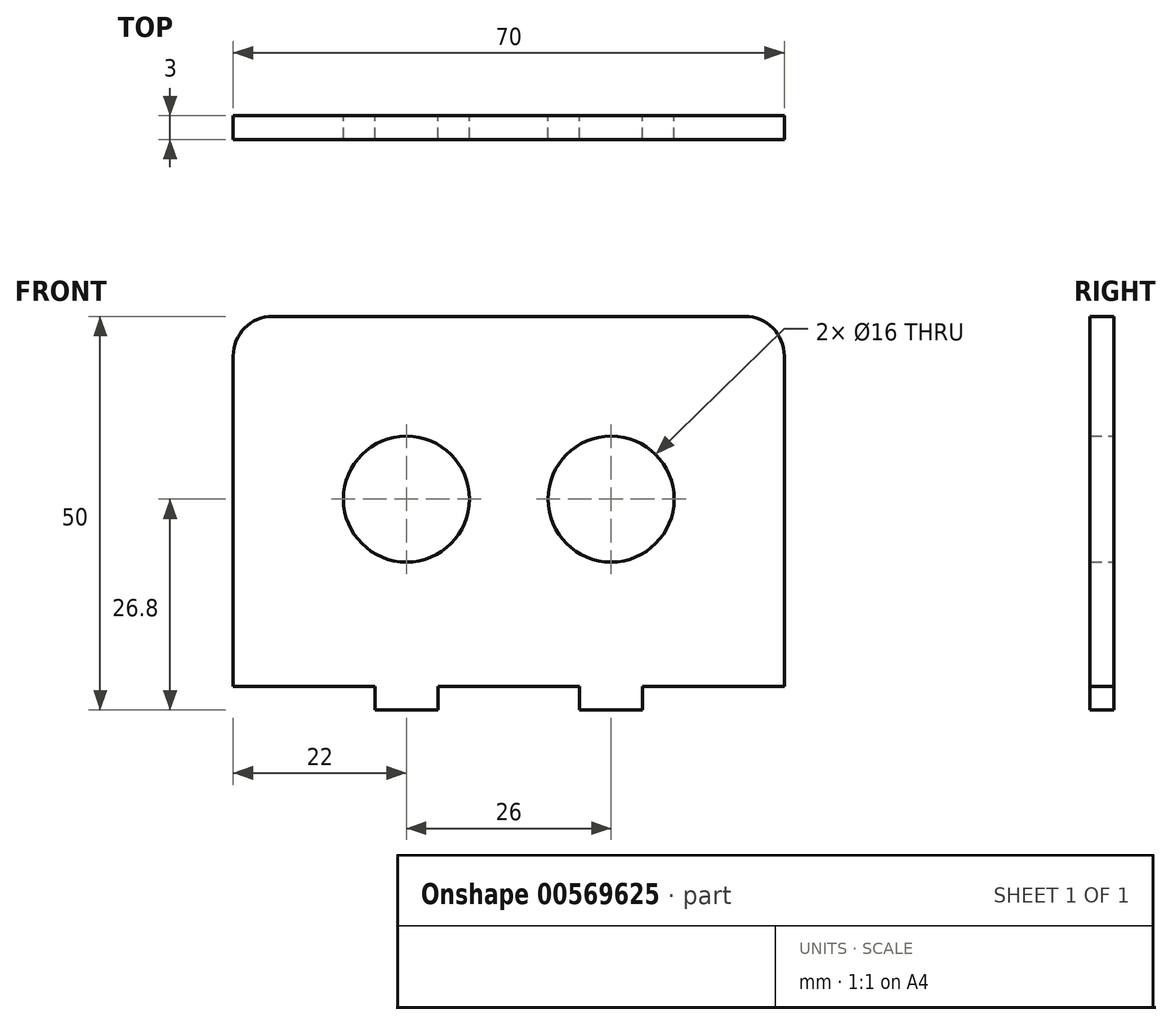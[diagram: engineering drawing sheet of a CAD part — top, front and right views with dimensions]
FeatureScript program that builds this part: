
annotation { "Feature Type Name" : "Feature", "Feature Type Description" : "" }
export const myFeature = defineFeature(function(context is Context, id is Id, definition is map)
    precondition{}
    {
        {
            var Q0;
            Q0=qCreatedBy(makeId("Front.planeOp"),FACE);
            var sketch = newSketch(context, id + "F0", { "sketchPlane" : qUnion([Q0])});
            skLineSegment(sketch, "E0.bottom", {"start": v(-34, 23.2) * mm, "end": v(26, 23.2) * mm});
            skLineSegment(sketch, "E0.top", {"start": v(-21, -26.8) * mm, "end": v(-13, -26.8) * mm});
            skLineSegment(sketch, "E0.left", {"start": v(-39, 18.2) * mm, "end": v(-39, -23.8) * mm});
            skLineSegment(sketch, "E0.right", {"start": v(31, 18.2) * mm, "end": v(31, -26.8) * mm});
            skCircle(sketch, "E1", {"center": v(-17, 0) * mm, "radius": 8 * mm});
            skCircle(sketch, "E2", {"center": v(9, 0) * mm, "radius": 8 * mm});
            skPoint(sketch, "E3.visualSharp", {"position": v(-39, 23.2) * mm});
            skArc(sketch, "E3.filletArc", {"start": v(-34, 23.2) * mm, "mid": v(-37.54, 21.74) * mm, "end": v(-39, 18.2) * mm});
            skPoint(sketch, "E4.visualSharp", {"position": v(31, 23.2) * mm});
            skArc(sketch, "E4.filletArc", {"start": v(31, 18.2) * mm, "mid": v(29.54, 21.74) * mm, "end": v(26, 23.2) * mm});
            skLineSegment(sketch, "E5", {"start": v(45.92, -19.01) * mm, "end": v(45.92, -19.01) * mm});
            skLineSegment(sketch, "E6", {"start": v(-44.57, -23.8) * mm, "end": v(-21, -23.8) * mm, "construction": true});
            skLineSegment(sketch, "E7", {"start": v(-21, -23.8) * mm, "end": v(-21, -26.8) * mm});
            skLineSegment(sketch, "E8", {"start": v(-13, -23.8) * mm, "end": v(-13, -26.8) * mm});
            skLineSegment(sketch, "E9", {"start": v(5, -23.8) * mm, "end": v(5, -26.8) * mm});
            skLineSegment(sketch, "E10", {"start": v(5, -26.8) * mm, "end": v(5, -23.8) * mm});
            skLineSegment(sketch, "E11", {"start": v(13, -23.8) * mm, "end": v(13, -26.8) * mm});
            skPoint(sketch, "E12.orphan", {"position": v(-39, -26.8) * mm});
            skLineSegment(sketch, "E13.trimOffspring", {"start": v(5, -26.8) * mm, "end": v(13, -26.8) * mm});
            skLineSegment(sketch, "E14", {"start": v(-39, -23.8) * mm, "end": v(-21, -23.8) * mm});
            skLineSegment(sketch, "E15.trimOffspring", {"start": v(-13, -23.8) * mm, "end": v(5, -23.8) * mm, "construction": true});
            skLineSegment(sketch, "E16.trimOffspring", {"start": v(-13, -23.8) * mm, "end": v(5, -23.8) * mm});
            skLineSegment(sketch, "E17.trimOffspring", {"start": v(13, -23.8) * mm, "end": v(35.88, -23.8) * mm, "construction": true});
            skLineSegment(sketch, "E18.trimOffspring", {"start": v(13, -23.8) * mm, "end": v(31, -23.8) * mm});
            skSolve(sketch);
        }
        {
            var Q0;
            Q0=makeQuery(id+"F0.imprint","IMPRINT",FACE,{"disambiguationData":[TD([[makeQuery(id+"F0.imprint","IMPRINT",EDGE,{"derivedFrom":sQuery(id+"F0.wireOp",EDGE,"E0.bottom")}),-1.0]])]});
            extrude(context, id + "F1", {"entities" : qUnion([Q0]), "depth" : 3 * mm, "offsetDistance" : 25 * mm});
        }
        {
            var Q0;
            Q0 = qSketchRegion(id + "F0", true);
            extrude(context, id + "F2", {"entities" : qUnion([Q0]), "depth" : 25 * mm, "offsetDistance" : 25 * mm});
        }
        {
            var Q0;
            Q0=makeQuery(id+"F2.opExtrude","SWEPT_BODY",BODY,{"disambiguationData":[OSD([sQuery(id+"F0.wireOp",EDGE,"E0.bottom"),sQuery(id+"F0.wireOp",EDGE,"E0.top"),sQuery(id+"F0.wireOp",EDGE,"E0.left"),sQuery(id+"F0.wireOp",EDGE,"E0.right"),sQuery(id+"F0.wireOp",EDGE,"E1"),sQuery(id+"F0.wireOp",EDGE,"E2"),sQuery(id+"F0.wireOp",EDGE,"E3.filletArc"),sQuery(id+"F0.wireOp",EDGE,"E4.filletArc"),sQuery(id+"F0.wireOp",EDGE,"E7"),sQuery(id+"F0.wireOp",EDGE,"E8"),sQuery(id+"F0.wireOp",EDGE,"E10"),sQuery(id+"F0.wireOp",EDGE,"E11"),sQuery(id+"F0.wireOp",EDGE,"E13.trimOffspring"),sQuery(id+"F0.wireOp",EDGE,"E14"),sQuery(id+"F0.wireOp",EDGE,"E16.trimOffspring"),sQuery(id+"F0.wireOp",EDGE,"E18.trimOffspring")])]});
            deleteBodies(context, id + "F3", {"entities" : qUnion([Q0])});
        }
    });
